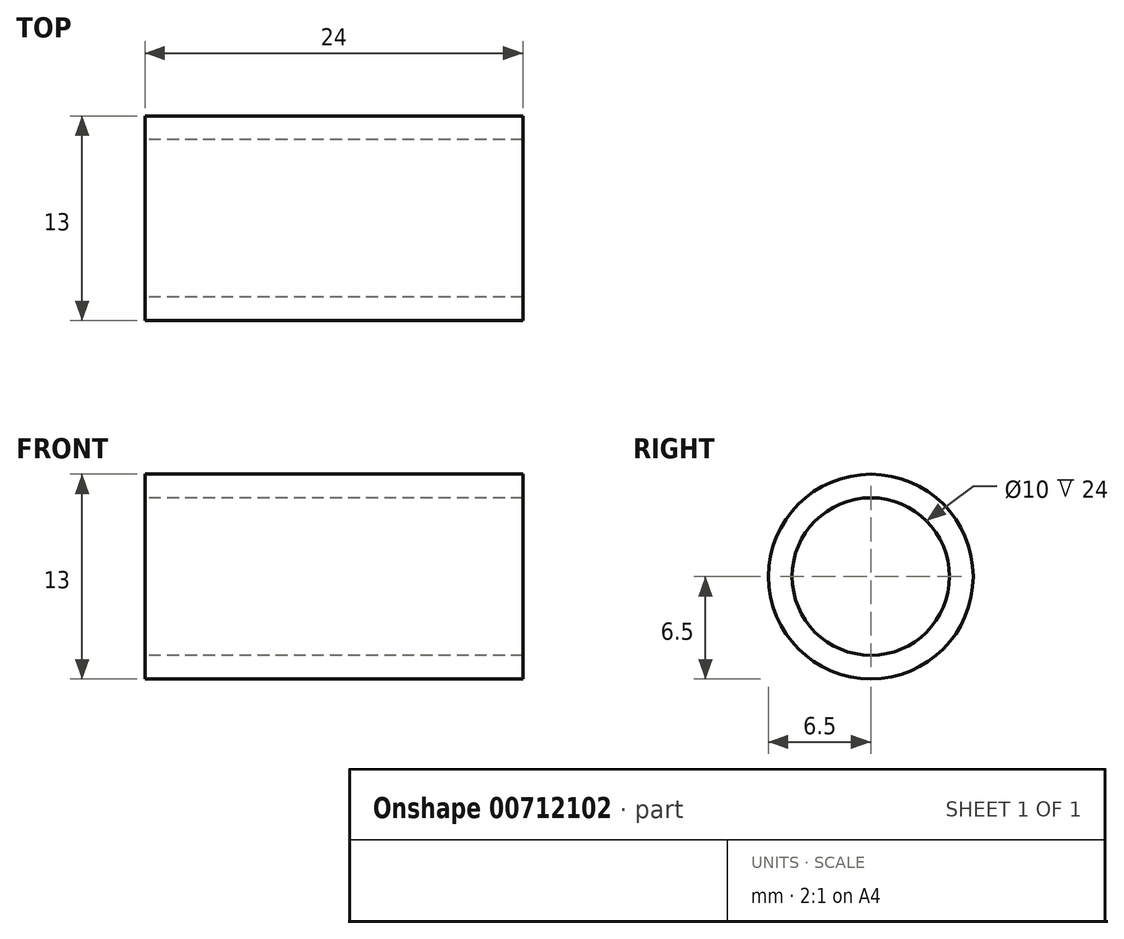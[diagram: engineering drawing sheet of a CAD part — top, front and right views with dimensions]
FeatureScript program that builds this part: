
annotation { "Feature Type Name" : "Feature", "Feature Type Description" : "" }
export const myFeature = defineFeature(function(context is Context, id is Id, definition is map)
    precondition{}
    {
        {
            var Q0;
            Q0=qCreatedBy(makeId("Right.planeOp"),FACE);
            var sketch = newSketch(context, id + "F0", { "sketchPlane" : qUnion([Q0])});
            skCircle(sketch, "E0", {"center": v(0, 0) * mm, "radius": 6.5 * mm});
            skCircle(sketch, "E1", {"center": v(0, 0) * mm, "radius": 5 * mm});
            skSolve(sketch);
        }
        {
            var Q0;
            Q0=makeQuery(id+"F0.imprint","IMPRINT",FACE,{"disambiguationData":[TD([[makeQuery(id+"F0.imprint","IMPRINT",EDGE,{"derivedFrom":sQuery(id+"F0.wireOp",EDGE,"E0")}),1.0]])]});
            extrude(context, id + "F1", {"entities" : qUnion([Q0]), "depth" : 24 * mm, "offsetDistance" : 25 * mm});
        }
    });
